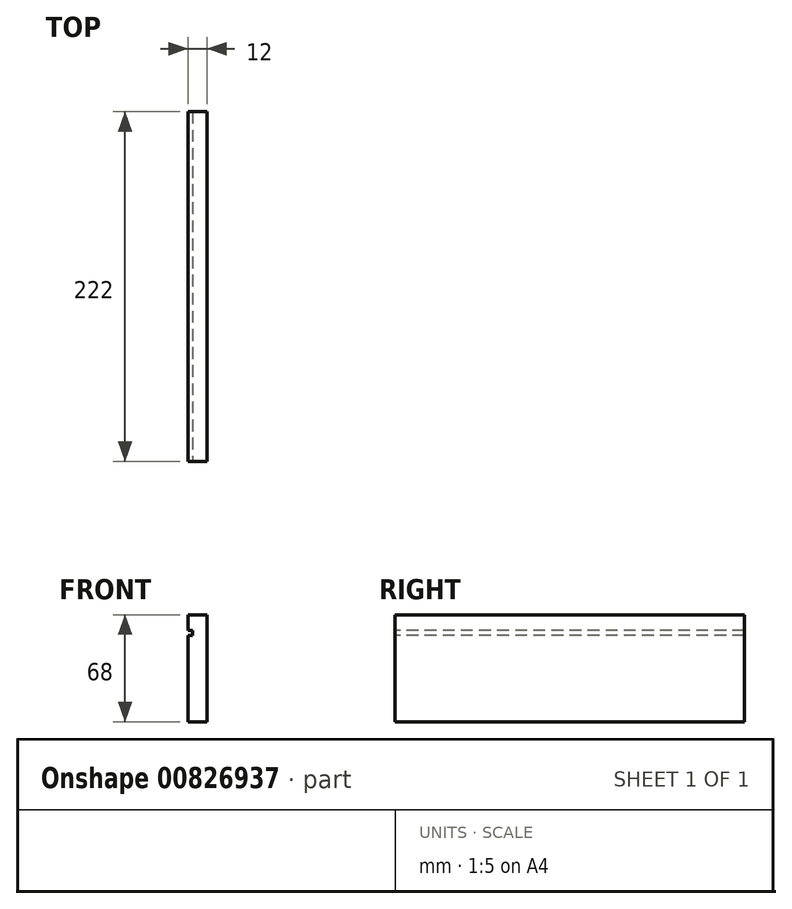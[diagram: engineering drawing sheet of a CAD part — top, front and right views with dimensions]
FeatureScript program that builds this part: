
annotation { "Feature Type Name" : "Feature", "Feature Type Description" : "" }
export const myFeature = defineFeature(function(context is Context, id is Id, definition is map)
    precondition{}
    {
        {
            var Q0;
            Q0=qCreatedBy(makeId("Right.planeOp"),FACE);
            var sketch = newSketch(context, id + "F0", { "sketchPlane" : qUnion([Q0])});
            skLineSegment(sketch, "E0.bottom", {"start": v(-111, 34) * mm, "end": v(111, 34) * mm});
            skLineSegment(sketch, "E0.top", {"start": v(-111, -34) * mm, "end": v(111, -34) * mm});
            skLineSegment(sketch, "E0.left", {"start": v(-111, 34) * mm, "end": v(-111, -34) * mm});
            skLineSegment(sketch, "E0.right", {"start": v(111, 34) * mm, "end": v(111, -34) * mm});
            skPoint(sketch, "E0.middle", {"position": v(0, 0) * mm});
            skSolve(sketch);
        }
        {
            var Q0;
            Q0 = qSketchRegion(id + "F0", true);
            extrude(context, id + "F1", {"entities" : qUnion([Q0]), "depth" : 12 * mm, "offsetDistance" : 25.4 * mm});
        }
        {
            var Q0;
            Q0=makeQuery(id+"F1.opExtrude","SWEPT_FACE",FACE,{"disambiguationData":[OSD([sQuery(id+"F0.wireOp",EDGE,"E0.left")])]});
            var sketch = newSketch(context, id + "F2", { "sketchPlane" : qUnion([Q0])});
            skLineSegment(sketch, "E1.bottom", {"start": v(0, 24) * mm, "end": v(3, 24) * mm});
            skLineSegment(sketch, "E1.top", {"start": v(0, 21) * mm, "end": v(3, 21) * mm});
            skLineSegment(sketch, "E1.left", {"start": v(0, 24) * mm, "end": v(0, 21) * mm});
            skLineSegment(sketch, "E1.right", {"start": v(3, 24) * mm, "end": v(3, 21) * mm});
            skSolve(sketch);
        }
        {
            var Q0;
            Q0 = qSketchRegion(id + "F2", true);
            extrude(context, id + "F3", {"entities" : qUnion([Q0]), "operationType" : NewBodyOperationType.REMOVE, "oppositeDirection" : true, "depth" : 300 * mm, "offsetDistance" : 25.4 * mm});
        }
    });
